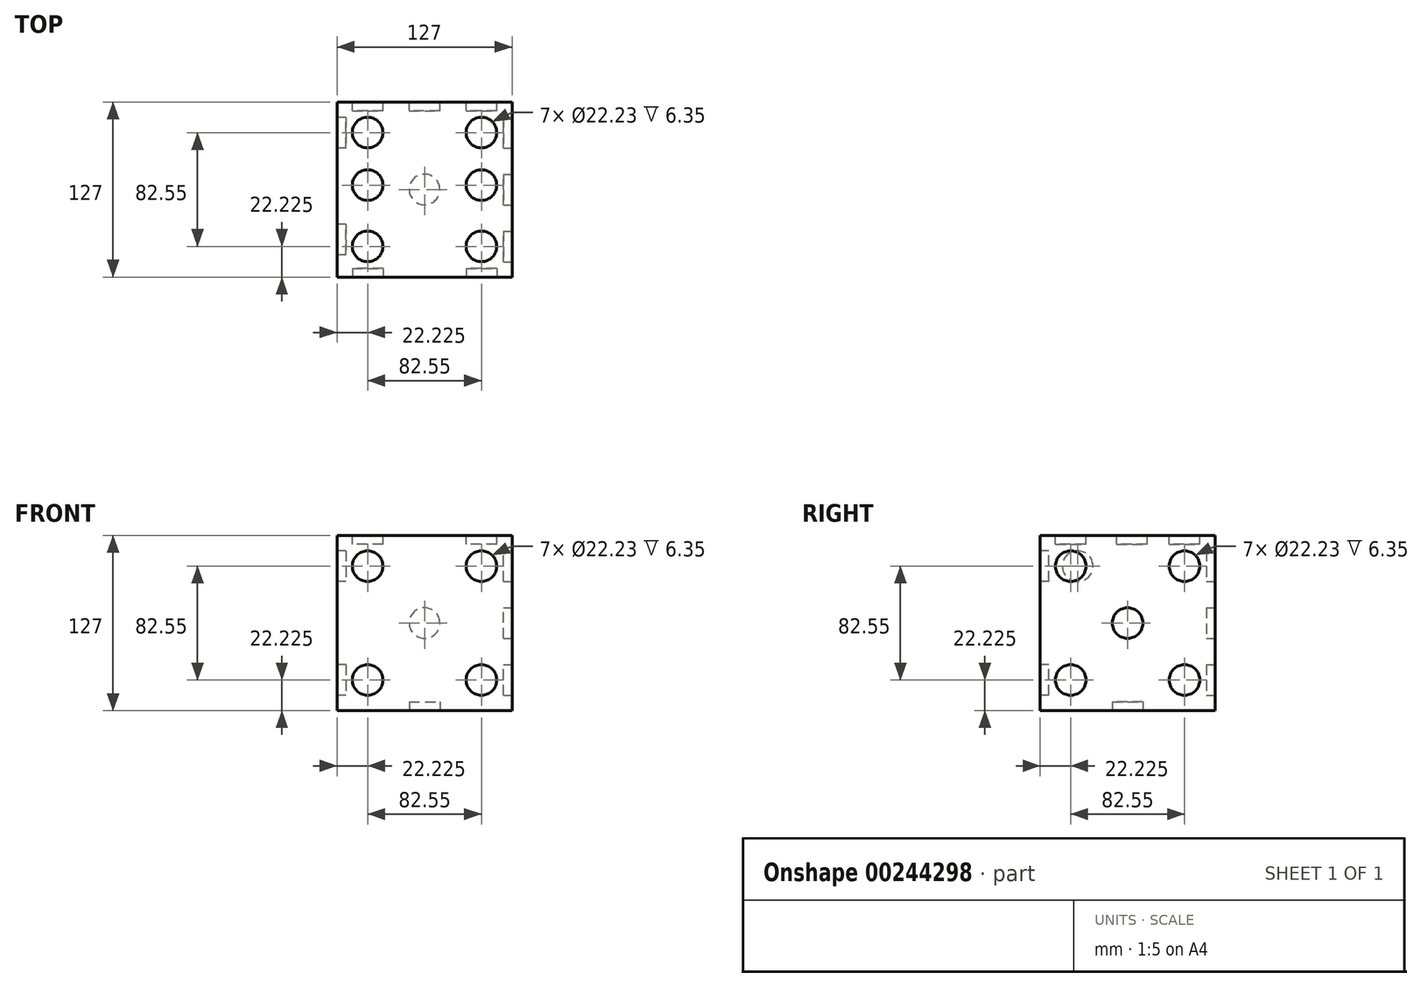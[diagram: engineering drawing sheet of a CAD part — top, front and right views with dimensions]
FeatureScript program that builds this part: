
annotation { "Feature Type Name" : "Feature", "Feature Type Description" : "" }
export const myFeature = defineFeature(function(context is Context, id is Id, definition is map)
    precondition{}
    {
        {
            var Q0;
            Q0=qCreatedBy(makeId("Top.planeOp"),FACE);
            var sketch = newSketch(context, id + "F0", { "sketchPlane" : qUnion([Q0])});
            skLineSegment(sketch, "E0.bottom", {"start": v(0, 0) * mm, "end": v(127, 0) * mm});
            skLineSegment(sketch, "E0.top", {"start": v(0, -127) * mm, "end": v(127, -127) * mm});
            skLineSegment(sketch, "E0.left", {"start": v(0, 0) * mm, "end": v(0, -127) * mm});
            skLineSegment(sketch, "E0.right", {"start": v(127, 0) * mm, "end": v(127, -127) * mm});
            skSolve(sketch);
        }
        {
            var Q0;
            Q0 = qSketchRegion(id + "F0", true);
            extrude(context, id + "F1", {"entities" : qUnion([Q0]), "depth" : 127 * mm});
        }
        {
            var Q0;
            Q0=makeQuery(id+"F1.opExtrude","CAP_FACE",FACE,{"disambiguationData":[OSD([sQuery(id+"F0.wireOp",EDGE,"E0.bottom"),sQuery(id+"F0.wireOp",EDGE,"E0.top"),sQuery(id+"F0.wireOp",EDGE,"E0.left"),sQuery(id+"F0.wireOp",EDGE,"E0.right")])],"isStart":true});
            var sketch = newSketch(context, id + "F2", { "sketchPlane" : qUnion([Q0])});
            skCircle(sketch, "E1", {"center": v(63.5, 63.5) * mm, "radius": 11.11 * mm});
            skSolve(sketch);
        }
        {
            var Q0;
            Q0=makeQuery(id+"F2.imprint","IMPRINT",FACE,{"disambiguationData":[TD([[makeQuery(id+"F2.imprint","IMPRINT",EDGE,{"derivedFrom":sQuery(id+"F2.wireOp",EDGE,"E1")}),1.0]])]});
            extrude(context, id + "F3", {"entities" : qUnion([Q0]), "operationType" : NewBodyOperationType.REMOVE, "oppositeDirection" : true, "depth" : 6.35 * mm});
        }
        {
            var Q0;
            Q0=makeQuery(id+"F1.opExtrude","SWEPT_FACE",FACE,{"disambiguationData":[OSD([sQuery(id+"F0.wireOp",EDGE,"E0.left")])]});
            var sketch = newSketch(context, id + "F4", { "sketchPlane" : qUnion([Q0])});
            skCircle(sketch, "E2", {"center": v(99.73, 104.78) * mm, "radius": 11.11 * mm});
            skCircle(sketch, "E3", {"center": v(22.23, 22.22) * mm, "radius": 11.11 * mm});
            skSolve(sketch);
        }
        {
            var Q0;
            Q0 = qSketchRegion(id + "F4", true);
            extrude(context, id + "F5", {"entities" : qUnion([Q0]), "operationType" : NewBodyOperationType.REMOVE, "oppositeDirection" : true, "depth" : 6.35 * mm});
        }
        {
            var Q0;
            Q0=makeQuery(id+"F1.opExtrude","SWEPT_FACE",FACE,{"disambiguationData":[OSD([sQuery(id+"F0.wireOp",EDGE,"E0.bottom")])]});
            var sketch = newSketch(context, id + "F6", { "sketchPlane" : qUnion([Q0])});
            skLineSegment(sketch, "E4", {"start": v(0, 127) * mm, "end": v(-127, 0) * mm, "construction": true});
            skCircle(sketch, "E5", {"center": v(-22.22, 104.78) * mm, "radius": 11.11 * mm});
            skCircle(sketch, "E6", {"center": v(-63.5, 63.5) * mm, "radius": 11.11 * mm});
            skCircle(sketch, "E7", {"center": v(-104.78, 22.23) * mm, "radius": 11.11 * mm});
            skSolve(sketch);
        }
        {
            var Q0;
            Q0 = qSketchRegion(id + "F6", true);
            extrude(context, id + "F7", {"entities" : qUnion([Q0]), "operationType" : NewBodyOperationType.REMOVE, "oppositeDirection" : true, "depth" : 6.35 * mm});
        }
        {
            var Q0;
            Q0=makeQuery(id+"F1.opExtrude","CAP_FACE",FACE,{"disambiguationData":[OSD([sQuery(id+"F0.wireOp",EDGE,"E0.bottom"),sQuery(id+"F0.wireOp",EDGE,"E0.top"),sQuery(id+"F0.wireOp",EDGE,"E0.left"),sQuery(id+"F0.wireOp",EDGE,"E0.right")])],"isStart":false});
            var sketch = newSketch(context, id + "F8", { "sketchPlane" : qUnion([Q0])});
            skCircle(sketch, "E8", {"center": v(22.23, -22.23) * mm, "radius": 11.11 * mm});
            skCircle(sketch, "E9", {"center": v(22.23, -60.33) * mm, "radius": 11.11 * mm});
            skCircle(sketch, "E10", {"center": v(22.23, -104.78) * mm, "radius": 11.11 * mm});
            skCircle(sketch, "E11", {"center": v(104.78, -22.23) * mm, "radius": 11.11 * mm});
            skCircle(sketch, "E12", {"center": v(104.78, -60.33) * mm, "radius": 11.11 * mm});
            skCircle(sketch, "E13", {"center": v(104.78, -104.78) * mm, "radius": 11.11 * mm});
            skSolve(sketch);
        }
        {
            var Q0;
            Q0=makeQuery(id+"F8.imprint","IMPRINT",FACE,{"disambiguationData":[TD([[makeQuery(id+"F8.imprint","IMPRINT",EDGE,{"derivedFrom":sQuery(id+"F8.wireOp",EDGE,"E8")}),1.0]])]});
            var Q1;
            Q1=makeQuery(id+"F8.imprint","IMPRINT",FACE,{"disambiguationData":[TD([[makeQuery(id+"F8.imprint","IMPRINT",EDGE,{"derivedFrom":sQuery(id+"F8.wireOp",EDGE,"E9")}),1.0]])]});
            var Q2;
            Q2=makeQuery(id+"F8.imprint","IMPRINT",FACE,{"disambiguationData":[TD([[makeQuery(id+"F8.imprint","IMPRINT",EDGE,{"derivedFrom":sQuery(id+"F8.wireOp",EDGE,"E10")}),1.0]])]});
            var Q3;
            Q3=makeQuery(id+"F8.imprint","IMPRINT",FACE,{"disambiguationData":[TD([[makeQuery(id+"F8.imprint","IMPRINT",EDGE,{"derivedFrom":sQuery(id+"F8.wireOp",EDGE,"E12")}),1.0]])]});
            var Q4;
            Q4=makeQuery(id+"F8.imprint","IMPRINT",FACE,{"disambiguationData":[TD([[makeQuery(id+"F8.imprint","IMPRINT",EDGE,{"derivedFrom":sQuery(id+"F8.wireOp",EDGE,"E13")}),1.0]])]});
            var Q5;
            Q5=makeQuery(id+"F8.imprint","IMPRINT",FACE,{"disambiguationData":[TD([[makeQuery(id+"F8.imprint","IMPRINT",EDGE,{"derivedFrom":sQuery(id+"F8.wireOp",EDGE,"E11")}),1.0]])]});
            extrude(context, id + "F9", {"entities" : qUnion([Q0, Q1, Q2, Q3, Q4, Q5]), "operationType" : NewBodyOperationType.REMOVE, "oppositeDirection" : true, "depth" : 6.35 * mm});
        }
        {
            var Q0;
            Q0=makeQuery(id+"F1.opExtrude","SWEPT_FACE",FACE,{"disambiguationData":[OSD([sQuery(id+"F0.wireOp",EDGE,"E0.top")])]});
            var sketch = newSketch(context, id + "F10", { "sketchPlane" : qUnion([Q0])});
            skCircle(sketch, "E14", {"center": v(104.78, 22.22) * mm, "radius": 11.11 * mm});
            skCircle(sketch, "E15", {"center": v(104.78, 104.78) * mm, "radius": 11.11 * mm});
            skCircle(sketch, "E16", {"center": v(22.23, 104.78) * mm, "radius": 11.11 * mm});
            skCircle(sketch, "E17", {"center": v(22.23, 22.22) * mm, "radius": 11.11 * mm});
            skSolve(sketch);
        }
        {
            var Q0;
            Q0 = qSketchRegion(id + "F10", true);
            extrude(context, id + "F11", {"entities" : qUnion([Q0]), "operationType" : NewBodyOperationType.REMOVE, "oppositeDirection" : true, "depth" : 6.35 * mm});
        }
        {
            var Q0;
            Q0=makeQuery(id+"F1.opExtrude","SWEPT_FACE",FACE,{"disambiguationData":[OSD([sQuery(id+"F0.wireOp",EDGE,"E0.right")])]});
            var sketch = newSketch(context, id + "F12", { "sketchPlane" : qUnion([Q0])});
            skLineSegment(sketch, "E18", {"start": v(0, 127) * mm, "end": v(-127, 0) * mm});
            skCircle(sketch, "E19", {"center": v(-63.5, 63.5) * mm, "radius": 11.11 * mm});
            skCircle(sketch, "E20", {"center": v(-104.78, 22.23) * mm, "radius": 11.11 * mm});
            skCircle(sketch, "E21", {"center": v(-22.23, 104.77) * mm, "radius": 11.11 * mm});
            skCircle(sketch, "E22", {"center": v(-22.23, 22.22) * mm, "radius": 11.11 * mm});
            skCircle(sketch, "E23", {"center": v(-104.78, 104.78) * mm, "radius": 11.11 * mm});
            skSolve(sketch);
        }
        {
            var Q0;
            Q0 = qSketchRegion(id + "F12", true);
            extrude(context, id + "F13", {"entities" : qUnion([Q0]), "operationType" : NewBodyOperationType.REMOVE, "oppositeDirection" : true, "depth" : 6.35 * mm});
        }
    });
